# Revit family: POR_Okyris2Clinic_A3809_BIM_FR
name_source: partatom
category: Plumbing Fixtures
revit_build: Autodesk Revit 2017 (Build: 20160225_1515(x64)
units: mm (PartAtom-declared; Revit-internal decimal feet)

## family parameters
Always vertical = No
Cut with Voids When Loaded = No
OmniClass Number = 23.45.55.00
OmniClass Title = Sanitary Faucets, Wastes
Part Type = Normal
Room Calculation Point = No
Round Connector Dimension = Use Diameter
Shared = No
Work Plane-Based = No

## types (1)
- A3809NU - OKYRIS 2 CLINIC - Boîtier électronique secteur apparent indépendant
    Accessoires = http://www.porcher.com
    Auteur = Ideal Standard
    BIMobject main category = Sanitary
    BIMobject main category code = sanitary
    BOSUseNativeGeometries = 1
    Bim-NomDuProjet = POR_Porcher_Taps_A3809NU
    Brand url = http://www.porcher.com
    Caractéristiques = Boîtier électronique secteur 
apparent indépendant - Pour plusieurs robinetteries montées en série 
sur secteur
1 électrovanne
Etanche IP 55 et antichoc
    CodeBarre = 4015413931625
    Conformité = NF
    ConseilsDInstallation = www.idealspec.fr
    Cost = 0 $
    Couleur = Chrome
    CoûtDeRemplacement = 0
    Date of publishing = 2018_05_23
    DateDeCréation = 2018_05_23
    Description = OKYRIS 2 CLINIC - Boîtier électronique secteur 
apparent indépendant
    Dimensions = 126 x 80 x 115 mm
    DuréeGarantie = ans
    DétailGarantie = Constructeur
    EAN code = https://4015413931625
    Edition number = 1
    Espace = Interne
    Forme = Complexe
    Hauteur = 115 mm  [stored 0.377297 ft]
    IFC Classification = Sanitary Terminal
    IfcExportAs = IfcSanitaryTerminalType
    IfcExportType = Taps & Mixers
    InformationsProduit = www.idealspec.fr
    Installation instructions = http://www.idealspec.fr
    Largeur = 126 mm
    Longueur = 80 mm
    Manufacturer name = Porcher
    Marque = PORCHER
    Material main = Sanitary brassware
    Matériel = Sanitary brassware
    Model = A3809NU
    NBS Reference Code = 35-79-95
    NBS Reference Description = Wash Basin And Trough Water Supply Fittings
    Nom = POR_Porcher_Taps_A3809NU
    Nominal height = 130
    Nominal width = 200
    OmniClass Code = 23-19 25 13 21 17
    OmniClass Description = Fittings
    PerformanceAccessibilité = NF
    PoidsNet = 1.1 Kg
    Product Guid = f40a63e1-fc64-41d3-9f3d-32453108c592
    Product SKU = A3809
    Product certification = http://www.idealspec.fr
    Product data url = https://bimobject.com
    Product family = OKYRIS 2 CLINIC
    Product group = Taps & Mixers
    Product name = OKYRIS 2 CLINIC - Boîtier électronique secteur 
apparent indépendant
    Product url = http://www.idealspec.fr
    Profondeur = 0 mm  [stored 0 ft]
    QR code = http://bimobject.com
    Raccordement = Plomberie
    Référence = A3809NU
    Révision = 1
    Technical description = http://www.idealspec.fr
    TypeDImmobilisation = Fixe
    URL = http://www.porcher.com
    Uniclass 1.4 Code = L8212
    Uniclass 1.4 Description = Fittings
    Uniclass 2.0 Code = PR-31-06
    Uniclass 2.0 Description = Bathing Fittings
    Uniclass 2015 Code = Pr_40_20_06
    Uniclass 2015 Name = Bathing fittings
    Uniclass2015Code = Pr_40_20_06
    Uniclass2015Title = Bathing fittings
    Uniclass2015Version = Products v1.1
    UnitéDeTemps = an
    UrlDuFabricant = http://www.porcher.com
    Version = 1
    Weight Net (Kg) = 1.1

note: [stored X ft] marks values corroborated as IEEE doubles in the binary element streams (Revit-internal decimal feet)

## geometry (parser evidence)
native form markers: Sweep x2
no freeform markers — native parametric forms only
